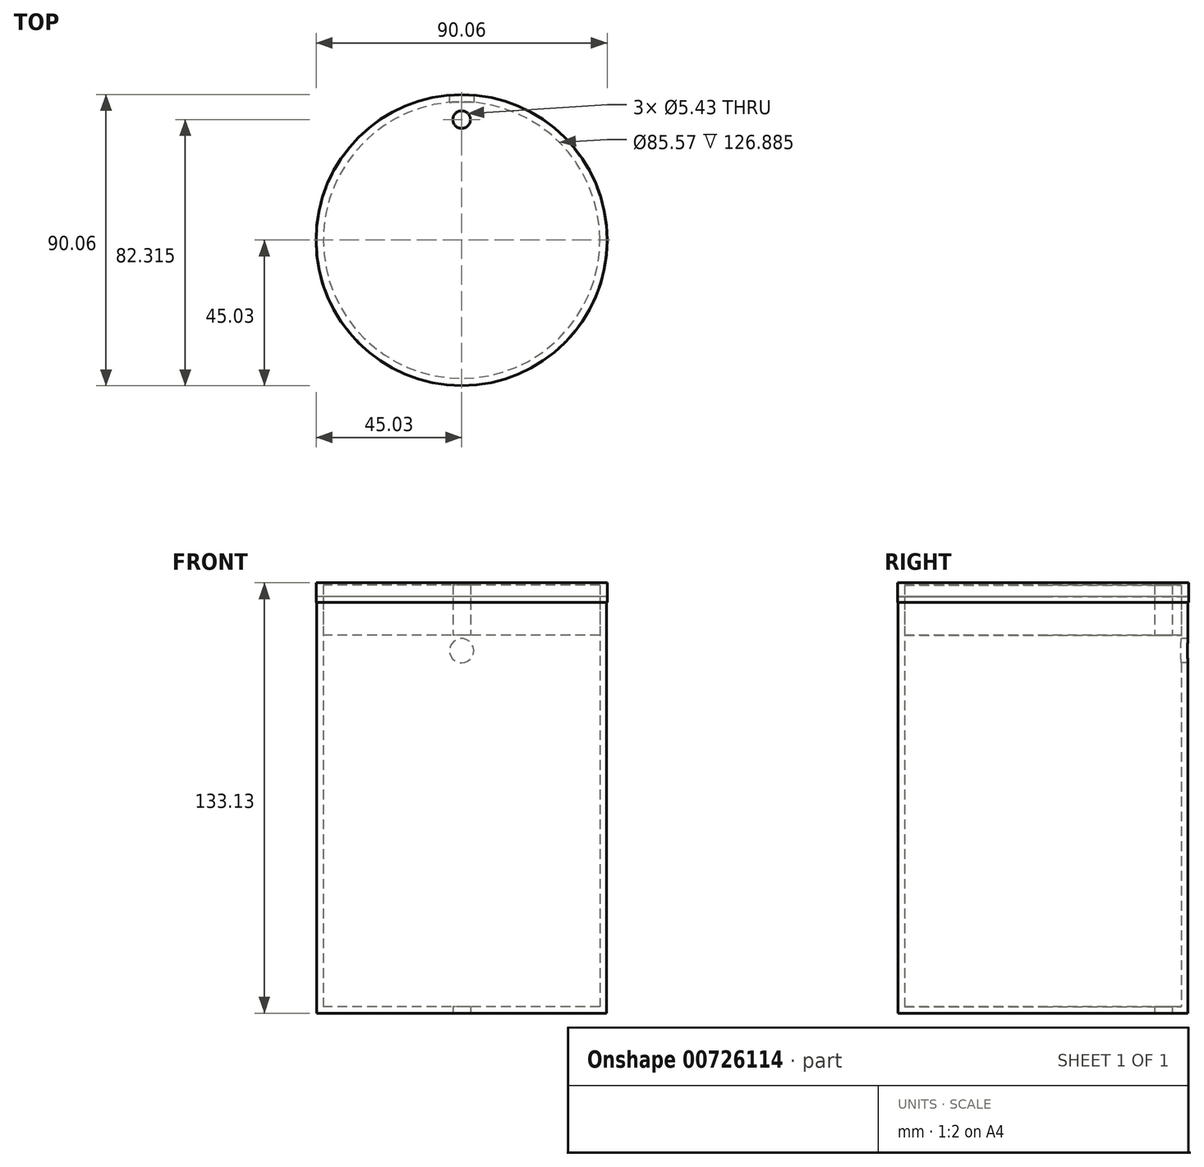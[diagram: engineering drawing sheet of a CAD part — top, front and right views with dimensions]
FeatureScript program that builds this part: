
annotation { "Feature Type Name" : "Feature", "Feature Type Description" : "" }
export const myFeature = defineFeature(function(context is Context, id is Id, definition is map)
    precondition{}
    {
        {
            var Q0;
            Q0=qCreatedBy(makeId("Top.planeOp"),FACE);
            var sketch = newSketch(context, id + "F0", { "sketchPlane" : qUnion([Q0])});
            skCircle(sketch, "E0", {"center": v(0, 0) * mm, "radius": 44.82 * mm});
            skSolve(sketch);
        }
        {
            var Q0;
            Q0 = qSketchRegion(id + "F0", true);
            extrude(context, id + "F1", {"entities" : qUnion([Q0]), "depth" : 106.76 * mm, "offsetDistance" : 25.4 * mm, "hasSecondDirection" : true, "secondDirectionOppositeDirection" : true, "secondDirectionDepth" : 22.15 * mm});
        }
        {
            var Q0;
            Q0=makeQuery(id+"F1.opExtrude","CAP_FACE",FACE,{"disambiguationData":[OSD([sQuery(id+"F0.wireOp",EDGE,"E0")])],"isStart":false});
            shell(context, id + "F2", {"entities" : qUnion([Q0]), "thickness" : 2.03 * mm});
        }
        {
            var Q0;
            Q0=qCreatedBy(makeId("Front.planeOp"),FACE);
            var sketch = newSketch(context, id + "F3", { "sketchPlane" : qUnion([Q0])});
            skCircle(sketch, "E1", {"center": v(0, 89.97) * mm, "radius": 3.77 * mm});
            skSolve(sketch);
        }
        {
            var Q0;
            Q0=makeQuery(id+"F3.imprint","IMPRINT",FACE,{"disambiguationData":[TD([[makeQuery(id+"F3.imprint","IMPRINT",EDGE,{"derivedFrom":sQuery(id+"F3.wireOp",EDGE,"E1")}),1.0]])]});
            extrude(context, id + "F4", {"entities" : qUnion([Q0]), "operationType" : NewBodyOperationType.REMOVE, "oppositeDirection" : true, "depth" : 59.9 * mm, "offsetDistance" : 25.4 * mm});
        }
        {
            var Q0;
            {var subQ0=sQuery(id+"F0.wireOp",EDGE,"E0");Q0=makeQuery(id+"F2.opShell","OFFSET_FACE",FACE,{"disambiguationData":[OSD([subQ0]),TDD([makeQuery(id+"F1.opExtrude","CAP_FACE",FACE,{"disambiguationData":[OSD([subQ0])],"isStart":true})])]});}
            extrude(context, id + "F5", {"entities" : qUnion([Q0]), "depth" : 105 * mm, "offsetDistance" : 25.4 * mm, "hasSecondDirection" : true, "secondDirectionOppositeDirection" : false, "secondDirectionDepth" : 91.43 * mm});
        }
        {
            var Q0;
            Q0=makeQuery(id+"F5.opExtrude","CAP_FACE",FACE,{"disambiguationData":[OSD([sQuery(id+"F0.wireOp",EDGE,"E0")])],"isStart":true});
            shell(context, id + "F6", {"entities" : qUnion([Q0]), "thickness" : 1.52 * mm});
        }
        {
            var Q0;
            Q0=qCreatedBy(makeId("Top.planeOp"),FACE);
            var sketch = newSketch(context, id + "F7", { "sketchPlane" : qUnion([Q0])});
            skCircle(sketch, "E2", {"center": v(0, 0) * mm, "radius": 45.03 * mm});
            skSolve(sketch);
        }
        {
            var Q0;
            Q0 = qSketchRegion(id + "F7", true);
            extrude(context, id + "F8", {"entities" : qUnion([Q0]), "depth" : 110.98 * mm, "offsetDistance" : 25.4 * mm, "hasSecondDirection" : true, "secondDirectionOppositeDirection" : false, "secondDirectionDepth" : 104.98 * mm});
        }
        {
            var Q0;
            Q0=makeQuery(id+"F5.opExtrude","CAP_FACE",FACE,{"disambiguationData":[OSD([sQuery(id+"F0.wireOp",EDGE,"E0")])],"isStart":false});
            extrude(context, id + "F9", {"entities" : qUnion([Q0]), "depth" : 25.4 * mm, "offsetDistance" : 25.4 * mm, "hasSecondDirection" : true, "secondDirectionOppositeDirection" : false, "secondDirectionDepth" : 9.9 * mm});
        }
        {
            var Q0;
            Q0=makeQuery(id+"F5.opExtrude","SWEPT_BODY",BODY,{"disambiguationData":[OSD([sQuery(id+"F0.wireOp",EDGE,"E0")])]});
            deleteBodies(context, id + "F10", {"entities" : qUnion([Q0])});
        }
        {
            var Q0;
            Q0=qCreatedBy(makeId("Top.planeOp"),FACE);
            var sketch = newSketch(context, id + "F11", { "sketchPlane" : qUnion([Q0])});
            skCircle(sketch, "E3", {"center": v(0, 37.28) * mm, "radius": 2.72 * mm});
            skSolve(sketch);
        }
        {
            var Q0;
            Q0=makeQuery(id+"F11.imprint","IMPRINT",FACE,{"disambiguationData":[TD([[makeQuery(id+"F11.imprint","IMPRINT",EDGE,{"derivedFrom":sQuery(id+"F11.wireOp",EDGE,"E3")}),1.0]])]});
            extrude(context, id + "F12", {"entities" : qUnion([Q0]), "operationType" : NewBodyOperationType.REMOVE, "depth" : 244.39 * mm, "offsetDistance" : 25.4 * mm, "hasSecondDirection" : true, "secondDirectionOppositeDirection" : true, "secondDirectionDepth" : 45.9 * mm});
        }
    });
